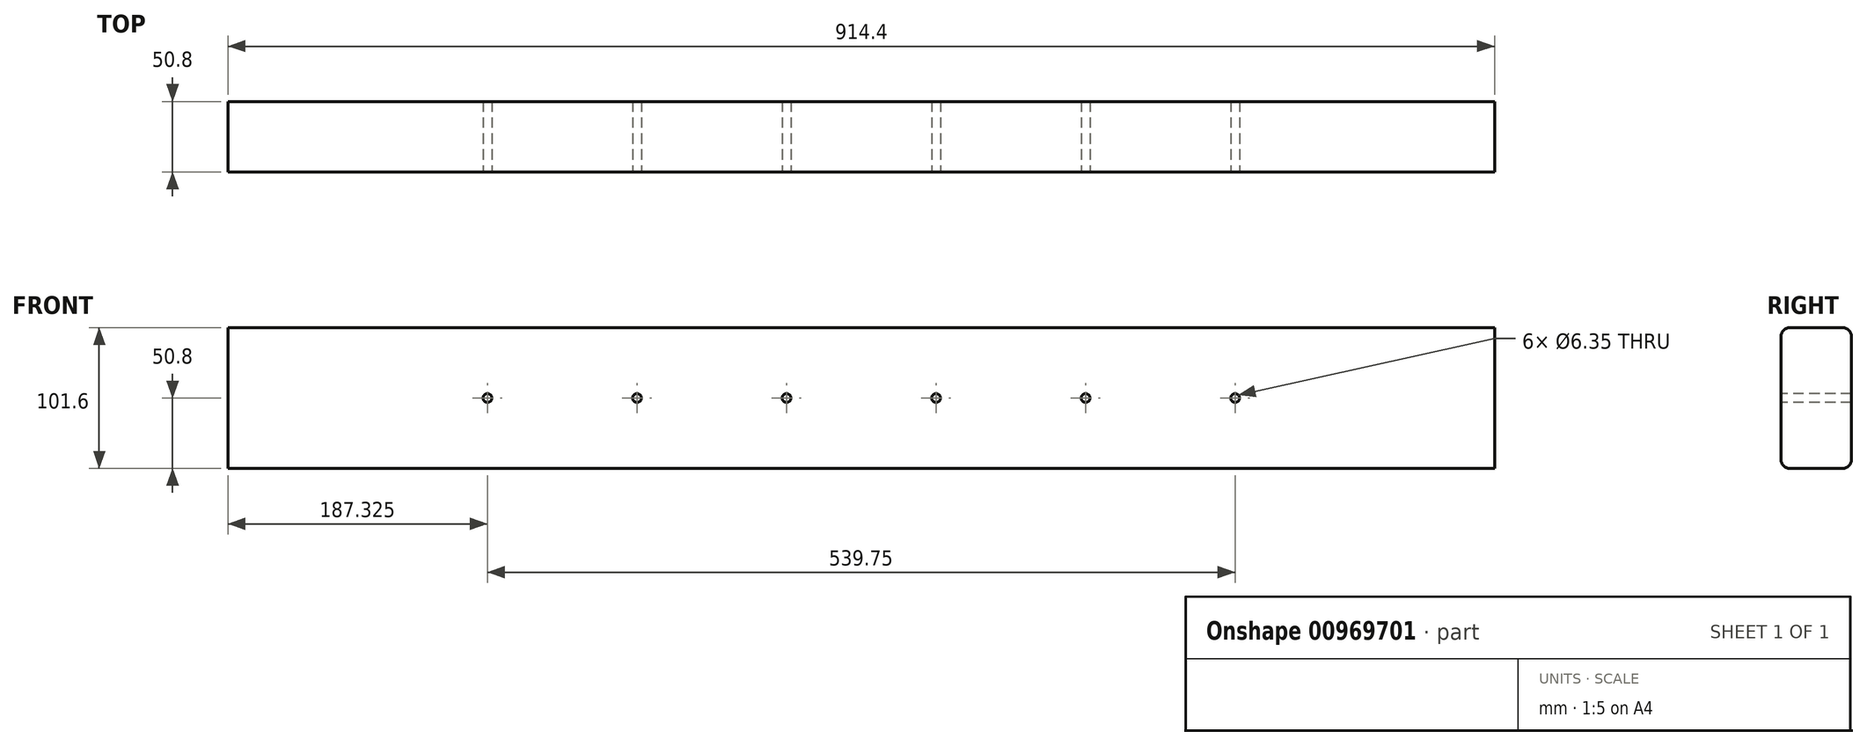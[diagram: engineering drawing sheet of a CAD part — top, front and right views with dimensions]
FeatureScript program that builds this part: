
annotation { "Feature Type Name" : "Feature", "Feature Type Description" : "" }
export const myFeature = defineFeature(function(context is Context, id is Id, definition is map)
    precondition{}
    {
        {
            var Q0;
            Q0=qCreatedBy(makeId("Right.planeOp"),FACE);
            var sketch = newSketch(context, id + "F0", { "sketchPlane" : qUnion([Q0])});
            skLineSegment(sketch, "E0.bottom", {"start": v(-25.4, -50.8) * mm, "end": v(25.4, -50.8) * mm});
            skLineSegment(sketch, "E0.top", {"start": v(-25.4, 50.8) * mm, "end": v(25.4, 50.8) * mm});
            skLineSegment(sketch, "E0.left", {"start": v(-25.4, -50.8) * mm, "end": v(-25.4, 50.8) * mm});
            skLineSegment(sketch, "E0.right", {"start": v(25.4, -50.8) * mm, "end": v(25.4, 50.8) * mm});
            skPoint(sketch, "E0.middle", {"position": v(0, 0) * mm});
            skSolve(sketch);
        }
        {
            var Q0;
            Q0=makeQuery(id+"F0.imprint","IMPRINT",FACE,{"disambiguationData":[TD([[makeQuery(id+"F0.imprint","IMPRINT",EDGE,{"derivedFrom":sQuery(id+"F0.wireOp",EDGE,"E0.bottom")}),1.0]])]});
            extrude(context, id + "F1", {"entities" : qUnion([Q0]), "endBound" : BoundingType.SYMMETRIC, "depth" : 914.4 * mm, "offsetDistance" : 25.4 * mm});
        }
        {
            var Q0;
            Q0=makeQuery(id+"F1.opExtrude","SWEPT_EDGE",EDGE,{"disambiguationData":[OSD([sQuery(id+"F0.wireOp",EDGE,"E0.bottom"),sQuery(id+"F0.wireOp",EDGE,"E0.left")])]});
            var Q1;
            Q1=makeQuery(id+"F1.opExtrude","SWEPT_EDGE",EDGE,{"disambiguationData":[OSD([sQuery(id+"F0.wireOp",EDGE,"E0.bottom"),sQuery(id+"F0.wireOp",EDGE,"E0.right")])]});
            var Q2;
            Q2=makeQuery(id+"F1.opExtrude","SWEPT_EDGE",EDGE,{"disambiguationData":[OSD([sQuery(id+"F0.wireOp",EDGE,"E0.top"),sQuery(id+"F0.wireOp",EDGE,"E0.left")])]});
            var Q3;
            Q3=makeQuery(id+"F1.opExtrude","SWEPT_EDGE",EDGE,{"disambiguationData":[OSD([sQuery(id+"F0.wireOp",EDGE,"E0.top"),sQuery(id+"F0.wireOp",EDGE,"E0.right")])]});
            fillet(context, id + "F2", {"entities" : qUnion([Q0, Q1, Q2, Q3]), "radius" : 6.35 * mm, "tangentPropagation" : true, "allowEdgeOverflow" : false});
        }
        {
            var Q0;
            Q0=makeQuery(id+"F1.opExtrude","SWEPT_FACE",FACE,{"disambiguationData":[OSD([sQuery(id+"F0.wireOp",EDGE,"E0.left")])]});
            var sketch = newSketch(context, id + "F3", { "sketchPlane" : qUnion([Q0])});
            skLineSegment(sketch, "E1.0.0", {"start": v(457.2, -44.45) * mm, "end": v(457.2, 44.45) * mm});
            skLineSegment(sketch, "E1.0.1", {"start": v(457.2, 44.45) * mm, "end": v(-457.2, 44.45) * mm});
            skLineSegment(sketch, "E1.0.2", {"start": v(-457.2, 44.45) * mm, "end": v(-457.2, -44.45) * mm});
            skLineSegment(sketch, "E1.0.3", {"start": v(-457.2, -44.45) * mm, "end": v(457.2, -44.45) * mm});
            skLineSegment(sketch, "E2", {"start": v(-381, 44.45) * mm, "end": v(-381, -44.45) * mm});
            skLineSegment(sketch, "E3", {"start": v(381, 44.45) * mm, "end": v(381, -44.45) * mm});
            skCircle(sketch, "E4", {"center": v(-269.88, 0) * mm, "radius": 3.18 * mm});
            skCircle(sketch, "E5", {"center": v(-161.93, 0) * mm, "radius": 3.18 * mm});
            skCircle(sketch, "E6", {"center": v(-53.98, 0) * mm, "radius": 3.18 * mm});
            skCircle(sketch, "E7", {"center": v(161.93, 0) * mm, "radius": 3.18 * mm});
            skCircle(sketch, "E8", {"center": v(53.98, 0) * mm, "radius": 3.18 * mm});
            skCircle(sketch, "E9", {"center": v(269.88, 0) * mm, "radius": 3.18 * mm});
            skSolve(sketch);
        }
        {
            var Q0;
            Q0=makeQuery(id+"F3.imprint","IMPRINT",FACE,{"disambiguationData":[TD([[makeQuery(id+"F3.imprint","IMPRINT",EDGE,{"derivedFrom":sQuery(id+"F3.wireOp",EDGE,"E4")}),1.0]])]});
            var Q1;
            Q1=makeQuery(id+"F3.imprint","IMPRINT",FACE,{"disambiguationData":[TD([[makeQuery(id+"F3.imprint","IMPRINT",EDGE,{"derivedFrom":sQuery(id+"F3.wireOp",EDGE,"E5")}),1.0]])]});
            var Q2;
            Q2=makeQuery(id+"F3.imprint","IMPRINT",FACE,{"disambiguationData":[TD([[makeQuery(id+"F3.imprint","IMPRINT",EDGE,{"derivedFrom":sQuery(id+"F3.wireOp",EDGE,"E6")}),1.0]])]});
            var Q3;
            Q3=makeQuery(id+"F3.imprint","IMPRINT",FACE,{"disambiguationData":[TD([[makeQuery(id+"F3.imprint","IMPRINT",EDGE,{"derivedFrom":sQuery(id+"F3.wireOp",EDGE,"E8")}),1.0]])]});
            var Q4;
            Q4=makeQuery(id+"F3.imprint","IMPRINT",FACE,{"disambiguationData":[TD([[makeQuery(id+"F3.imprint","IMPRINT",EDGE,{"derivedFrom":sQuery(id+"F3.wireOp",EDGE,"E7")}),1.0]])]});
            var Q5;
            Q5=makeQuery(id+"F3.imprint","IMPRINT",FACE,{"disambiguationData":[TD([[makeQuery(id+"F3.imprint","IMPRINT",EDGE,{"derivedFrom":sQuery(id+"F3.wireOp",EDGE,"E9")}),1.0]])]});
            extrude(context, id + "F4", {"entities" : qUnion([Q0, Q1, Q2, Q3, Q4, Q5]), "operationType" : NewBodyOperationType.REMOVE, "endBound" : BoundingType.UP_TO_NEXT, "oppositeDirection" : true, "depth" : 25.4 * mm, "offsetDistance" : 25.4 * mm});
        }
    });
